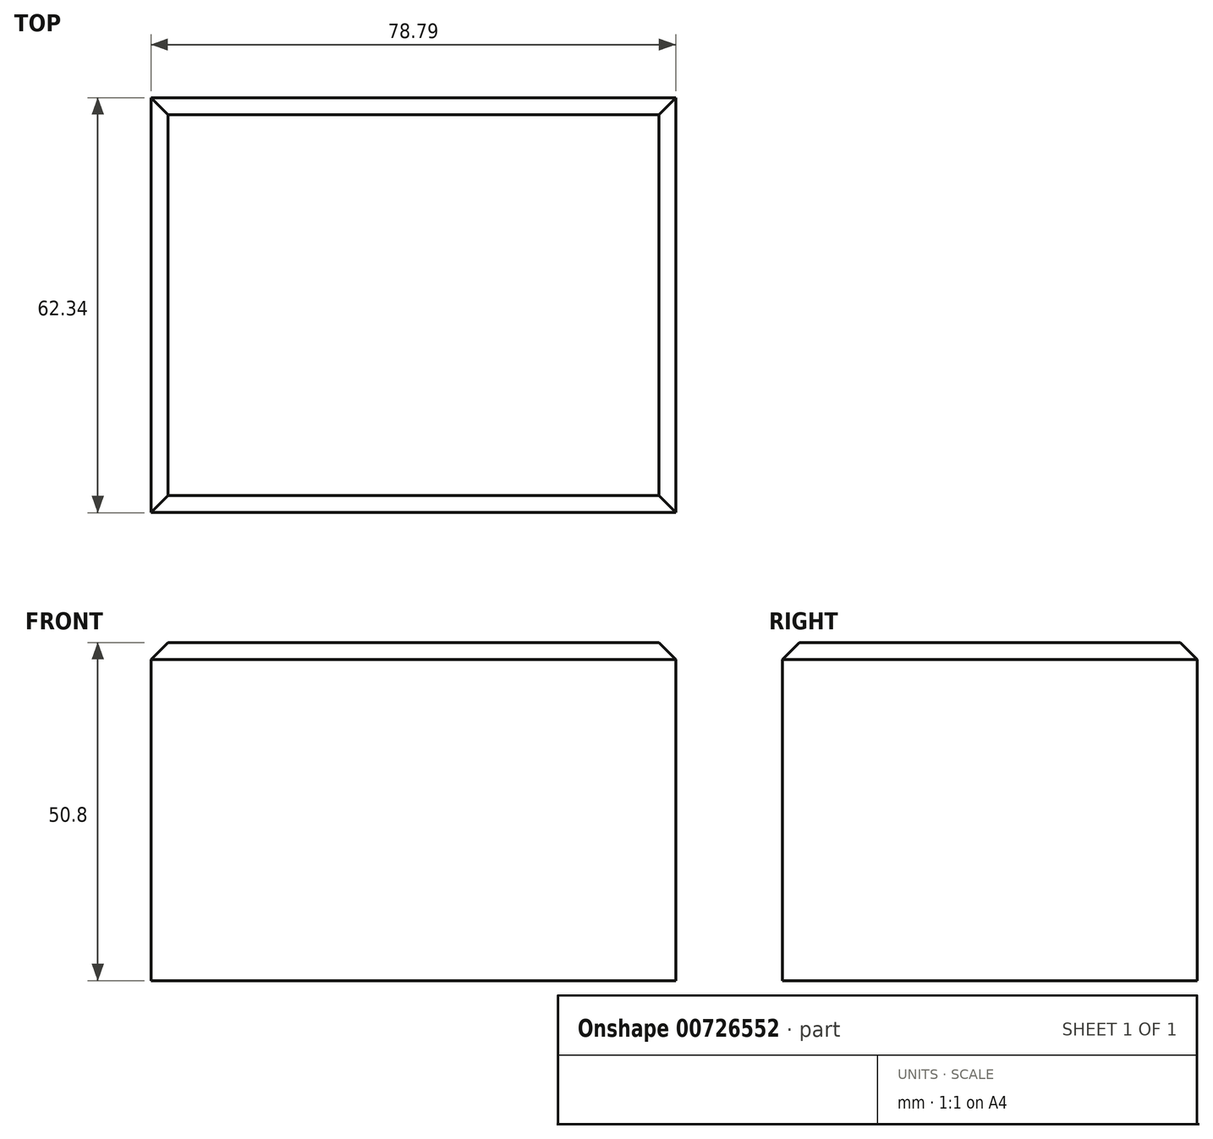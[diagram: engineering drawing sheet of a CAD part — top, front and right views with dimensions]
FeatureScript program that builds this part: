
annotation { "Feature Type Name" : "Feature", "Feature Type Description" : "" }
export const myFeature = defineFeature(function(context is Context, id is Id, definition is map)
    precondition{}
    {
        {
            var Q0;
            Q0=qCreatedBy(makeId("Top.planeOp"),FACE);
            var sketch = newSketch(context, id + "F0", { "sketchPlane" : qUnion([Q0])});
            skLineSegment(sketch, "E0.bottom", {"start": v(-41.2, 27.5) * mm, "end": v(37.59, 27.5) * mm});
            skLineSegment(sketch, "E0.top", {"start": v(-41.2, -34.83) * mm, "end": v(37.59, -34.83) * mm});
            skLineSegment(sketch, "E0.left", {"start": v(-41.2, 27.5) * mm, "end": v(-41.2, -34.83) * mm});
            skLineSegment(sketch, "E0.right", {"start": v(37.59, 27.5) * mm, "end": v(37.59, -34.83) * mm});
            skSolve(sketch);
        }
        {
            var Q0;
            Q0 = qSketchRegion(id + "F0", true);
            extrude(context, id + "F1", {"entities" : qUnion([Q0]), "depth" : 50.8 * mm, "offsetDistance" : 25.4 * mm});
        }
        {
            var Q0;
            Q0=makeQuery(id+"F1.opExtrude","CAP_FACE",FACE,{"disambiguationData":[OSD([sQuery(id+"F0.wireOp",EDGE,"E0.bottom"),sQuery(id+"F0.wireOp",EDGE,"E0.top"),sQuery(id+"F0.wireOp",EDGE,"E0.left"),sQuery(id+"F0.wireOp",EDGE,"E0.right")])],"isStart":false});
            chamfer(context, id + "F2", {"entities" : qUnion([Q0]), "chamferType" : ChamferType.TWO_OFFSETS, "width1" : 2.54 * mm, "oppositeDirection" : false, "width2" : 2.54 * mm, "tangentPropagation" : true});
        }
        {
            var Q0;
            Q0=makeQuery(id+"F1.opExtrude","CAP_FACE",FACE,{"disambiguationData":[OSD([sQuery(id+"F0.wireOp",EDGE,"E0.bottom"),sQuery(id+"F0.wireOp",EDGE,"E0.top"),sQuery(id+"F0.wireOp",EDGE,"E0.left"),sQuery(id+"F0.wireOp",EDGE,"E0.right")])],"isStart":false});
            var sketch = newSketch(context, id + "F3", { "sketchPlane" : qUnion([Q0])});
            skSolve(sketch);
        }
    });
